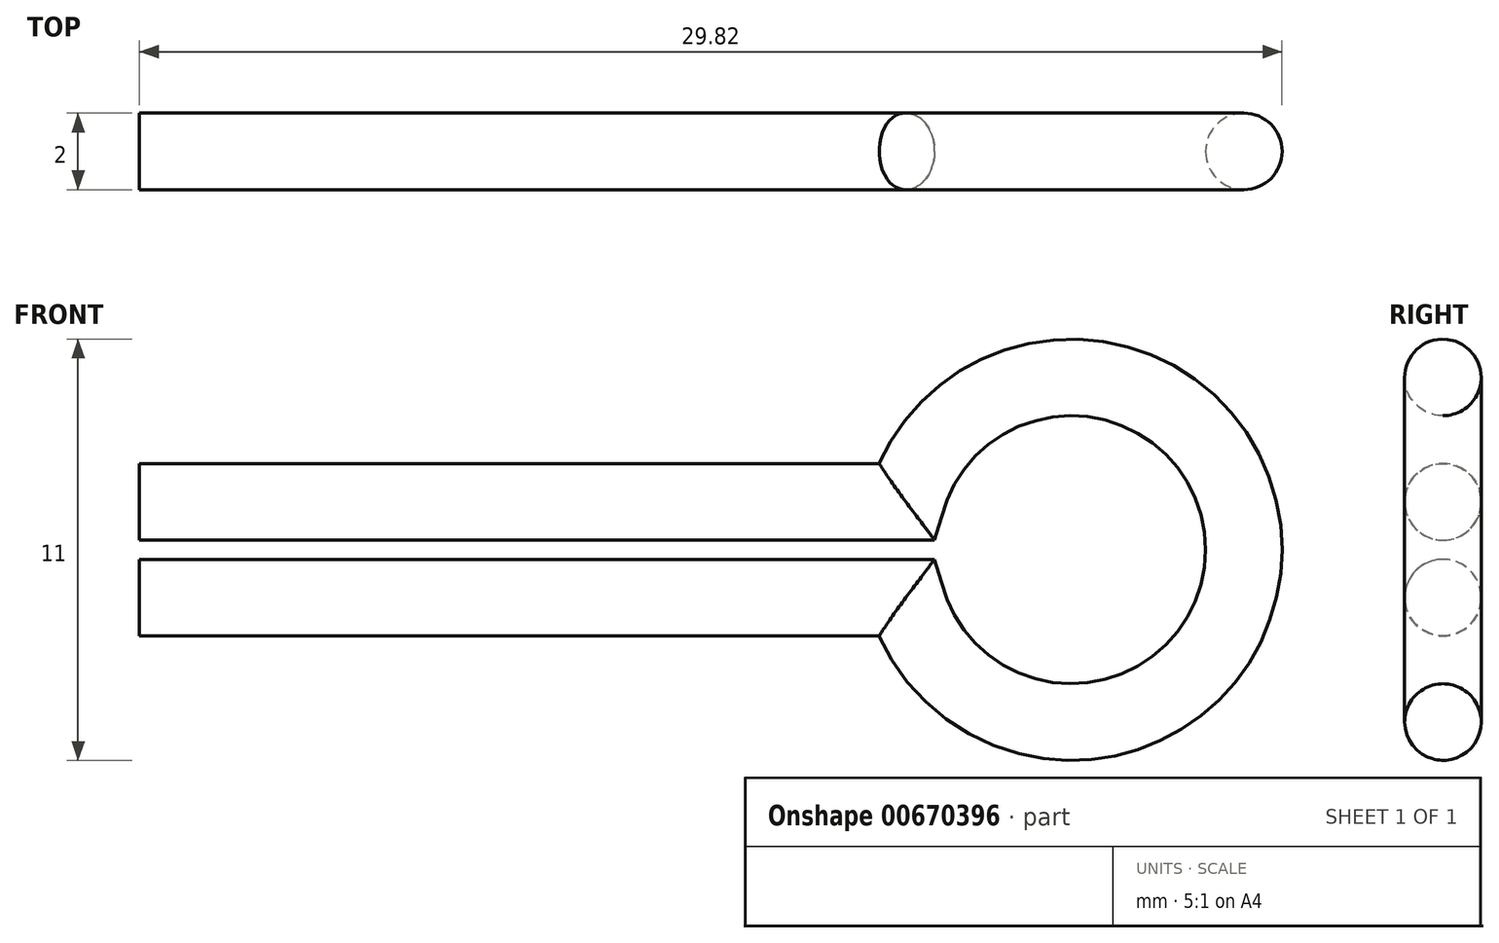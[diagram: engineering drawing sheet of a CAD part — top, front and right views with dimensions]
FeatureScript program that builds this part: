
annotation { "Feature Type Name" : "Feature", "Feature Type Description" : "" }
export const myFeature = defineFeature(function(context is Context, id is Id, definition is map)
    precondition{}
    {
        {
            var Q0;
            Q0=qCreatedBy(makeId("Front.planeOp"),FACE);
            var sketch = newSketch(context, id + "F0", { "sketchPlane" : qUnion([Q0])});
            skLineSegment(sketch, "E0", {"start": v(-15.5, 0) * mm, "end": v(16.42, 0) * mm, "construction": true});
            skLineSegment(sketch, "E1", {"start": v(-20, 1.25) * mm, "end": v(0, 1.25) * mm});
            skArc(sketch, "E2", {"start": v(0, -1.25) * mm, "mid": v(8.82, 0) * mm, "end": v(0, 1.25) * mm});
            skLineSegment(sketch, "E3.MirrorCS", {"start": v(-20, -1.25) * mm, "end": v(0, -1.25) * mm});
            skSolve(sketch);
        }
        {
            var Q0;
            Q0=qCreatedBy(makeId("Right.planeOp"),FACE);
            cPlane(context, id + "F1", {"entities" : qUnion([Q0]), "cplaneType" : CPlaneType.OFFSET, "offset" : 20 * mm, "oppositeDirection" : true, "width" : 150 * mm, "height" : 150 * mm});
        }
        {
            var Q0;
            Q0=qCreatedBy(id+"F1.planeOp",FACE);
            var sketch = newSketch(context, id + "F2", { "sketchPlane" : qUnion([Q0])});
            skCircle(sketch, "E4", {"center": v(0, 1.25) * mm, "radius": 1 * mm});
            skSolve(sketch);
        }
        {
            var Q0;
            Q0=makeQuery(id+"F2.imprint","IMPRINT",FACE,{"disambiguationData":[TD([[makeQuery(id+"F2.imprint","IMPRINT",EDGE,{"derivedFrom":sQuery(id+"F2.wireOp",EDGE,"E4")}),1.0]])]});
            var Q1;
            Q1=sQuery(id+"F0.wireOp",EDGE,"E1");
            var Q2;
            Q2=sQuery(id+"F0.wireOp",EDGE,"E2");
            var Q3;
            Q3=sQuery(id+"F0.wireOp",EDGE,"E3.MirrorCS");
            sweep(context, id + "F3", {"profiles" : qUnion([Q0]), "path" : qUnion([Q1, Q2, Q3])});
        }
    });
